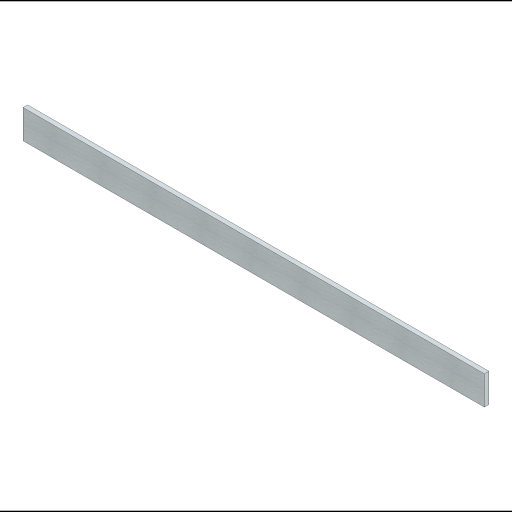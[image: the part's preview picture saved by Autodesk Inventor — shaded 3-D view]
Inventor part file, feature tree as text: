
AUTODESK INVENTOR PART (.ipt)
format: ipt  version: 2023 (Build 270158000, 158)  size: 112,640 bytes
history: native  units: in
note: dims shown in document units (in); Inventor stores cm internally (conversion verified against a paired STEP export)
features: extrude x1, sketch x1
ambient origin geometry x8: Origin, YZ Plane, XZ Plane, XY Plane, X Axis, Y Axis, Z Axis, Center Point
bodies: Solid1 (feature_tree)
feature tree (2):
  extrude  "Extrusion1"  Depth=3.0in
  sketch  "Sketch1"  dims[d0=48.0in d1=3.0in d2=0.47in d3=0.0in]
